# Revit family: Control_Unit-Lutron-Vive_PowPak_Relay_Module_SoftSwitch
name_source: partatom
category: Lighting Devices
revit_build: Autodesk Revit 2017 (Build: 20160720_1515(x64)
units: mm (PartAtom-declared; Revit-internal decimal feet)

## family parameters
Cut with Voids When Loaded = No
Host = Face
Maintain Annotation Orientation = Yes
OmniClass Number = 23.85.80.11.27
OmniClass Title = Lighting Controls
Part Type = Normal
Room Calculation Point = No
Round Connector Dimension = Use Radius
Shared = No

## types (4) — shared parameters
Assembly Code = D5020200
Bracket Offset = 0' - 0 3/16"
Bracket Thickness = 0' - 0 1/32"
Bracket Width = 0' - 0 1/4"
Capacity = 16 A
Connection Knob = 0' - 0 17/32"
Connection Knob Diameter = 0' - 0 1/2"
Connection Knob Radius = 0' - 0 1/4"
Default Elevation = 0' - 0"
Description = Vive PowPak Relay Module with Softswitch®
Device Material = Plastic - Lutron - White
Edge Radius = 0' - 0 1/4"
Front Panel Cutout Offset = 0' - 0 9/16"
Front Panel Left Edge = 0' - 0 11/32"
Front Panel Right Edge = 0' - 0 11/32"
Instruction Sheet Link = http://www.lutron.com
Label Secondary = COO
Manufacturer = Lutron Electronics Co., Inc
Manufacturer Fax Number = 610-282-1243
Maximum Operating Temperature = 131 °F
Minimum Operating Temperature = 32 °F
Number of Poles = 1
Overall Depth = 0' - 1 1/4"
Overall Height = 0' - 3 15/32"
Overall Width = 0' - 2 13/16"
Performance URL = http://www.lutron.com
Power = 1 W
Product Documentation Link = http://www.lutron.com
Product Name = Vive PowPak Relay Module with Softswitch
Product Page URL = http://www.lutron.com
Series = QS
URL = http://www.lutron.com
Version = 2017 - v1.0b
Video Link = https://www.youtube.com
Voltage = 120 V
Warranty URL = http://www.lutron.com
zero-valued in all types: Cost

## per-type parameters (varying)
| type | Current | Label 1 | Label 2 | Label Primary Visibility | Label Secondary Visibility |
| RMJS-16R-DV-B | 16 A | 16R | 2 | Yes | No |
| RMJS-5R-DV-B | 5 A | 5R | 2 | Yes | No |
| RMJS-16RCCO1DV-B | 16 A | 16R | 1 | No | Yes |
| RMJS-5RCCO1-DV-B | 5 A | 5R | 1 | No | Yes |

note: column(s) folded — value = type name in every type: Model

## geometry (parser evidence)
native form markers: Sweep x3
no freeform markers — native parametric forms only
